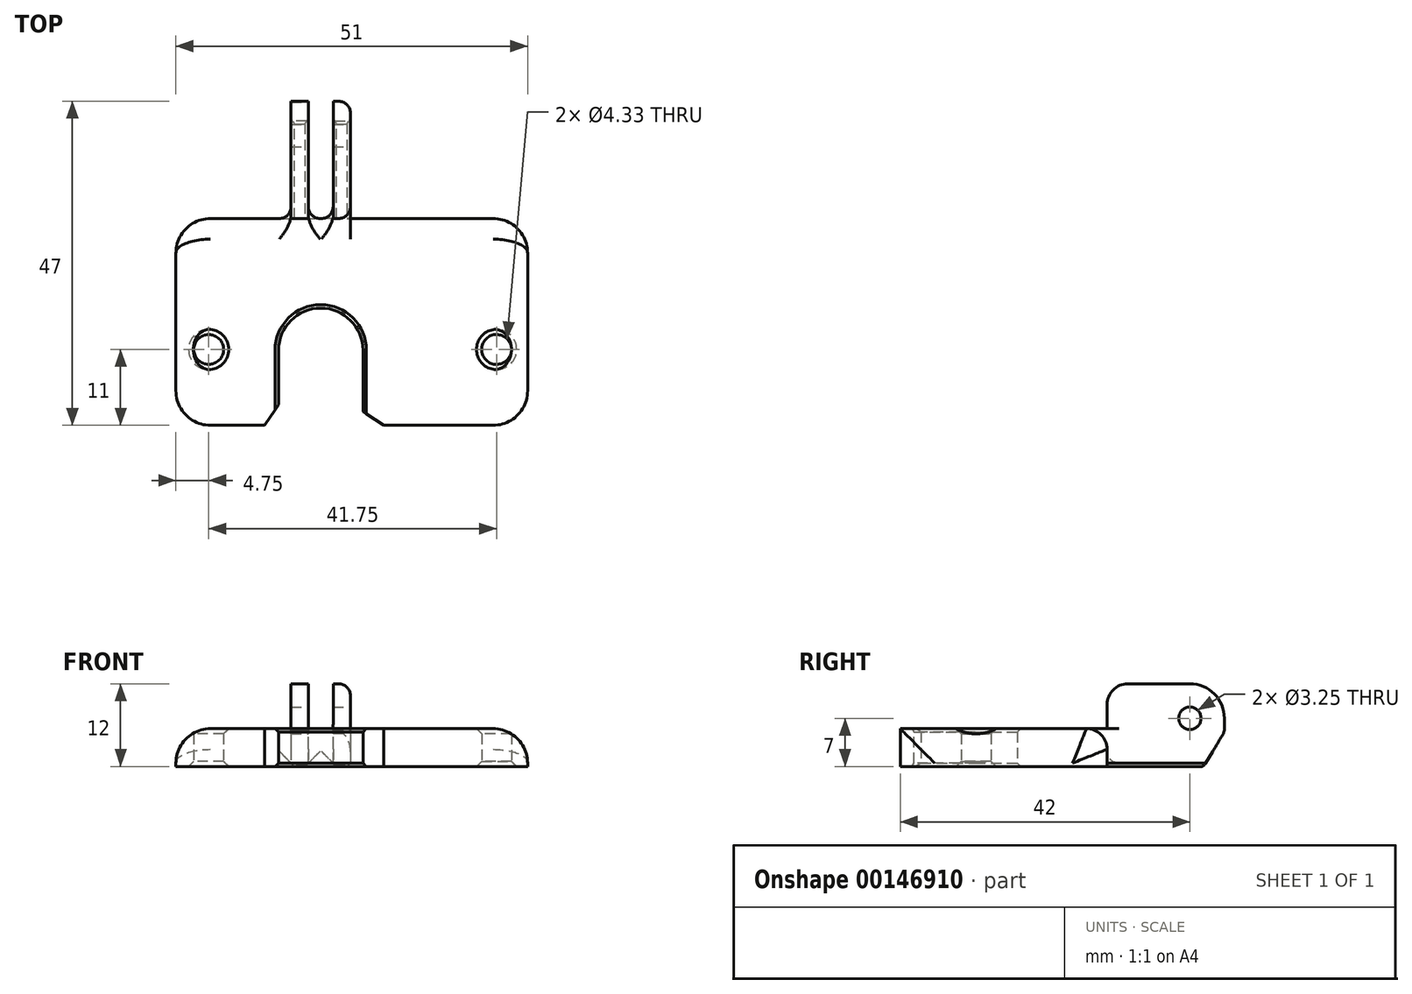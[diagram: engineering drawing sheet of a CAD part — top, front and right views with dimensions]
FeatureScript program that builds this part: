
annotation { "Feature Type Name" : "Feature", "Feature Type Description" : "" }
export const myFeature = defineFeature(function(context is Context, id is Id, definition is map)
    precondition{}
    {
        {
            var Q0;
            Q0=qCreatedBy(makeId("Top.planeOp"),FACE);
            var sketch = newSketch(context, id + "F0", { "sketchPlane" : qUnion([Q0])});
            skLineSegment(sketch, "E0.bottom", {"start": v(-25.5, 11) * mm, "end": v(25.5, 11) * mm});
            skLineSegment(sketch, "E0.top", {"start": v(-25.5, -11) * mm, "end": v(-10.62, -11) * mm});
            skLineSegment(sketch, "E0.left", {"start": v(-25.5, 11) * mm, "end": v(-25.5, -11) * mm});
            skLineSegment(sketch, "E0.right", {"start": v(25.5, 11) * mm, "end": v(25.5, -11) * mm});
            skArc(sketch, "E1", {"start": v(1.63, -0.13) * mm, "mid": v(-4.5, 6) * mm, "end": v(-10.62, -0.13) * mm});
            skLineSegment(sketch, "E2", {"start": v(-10.63, -0.13) * mm, "end": v(-10.62, -11) * mm});
            skLineSegment(sketch, "E3", {"start": v(1.63, -0.13) * mm, "end": v(1.63, -11) * mm});
            skLineSegment(sketch, "E4.trimOffspring", {"start": v(1.63, -11) * mm, "end": v(25.5, -11) * mm});
            skCircle(sketch, "E5", {"center": v(-20.75, 0) * mm, "radius": 2.17 * mm});
            skPoint(sketch, "E6.centerSnap0", {"position": v(-25.5, 0) * mm});
            skCircle(sketch, "E7", {"center": v(21, 0) * mm, "radius": 2.17 * mm});
            skSolve(sketch);
        }
        {
            var Q0;
            Q0 = qSketchRegion(id + "F0", true);
            extrude(context, id + "F1", {"entities" : qUnion([Q0]), "depth" : 5.5 * mm});
        }
        {
            var Q0;
            Q0=makeQuery(id+"F1.opExtrude","CAP_EDGE",EDGE,{"disambiguationData":[OSD([sQuery(id+"F0.wireOp",EDGE,"E5")])],"isStart":true});
            var Q1;
            Q1=makeQuery(id+"F1.opExtrude","CAP_EDGE",EDGE,{"disambiguationData":[OSD([sQuery(id+"F0.wireOp",EDGE,"E7")])],"isStart":true});
            var Q2;
            Q2=makeQuery(id+"F1.opExtrude","CAP_EDGE",EDGE,{"disambiguationData":[OSD([sQuery(id+"F0.wireOp",EDGE,"E7")])],"isStart":false});
            var Q3;
            Q3=makeQuery(id+"F1.opExtrude","CAP_EDGE",EDGE,{"disambiguationData":[OSD([sQuery(id+"F0.wireOp",EDGE,"E5")])],"isStart":false});
            chamfer(context, id + "F2", {"entities" : qUnion([Q0, Q1, Q2, Q3]), "width" : .75 * mm, "tangentPropagation" : true});
        }
        {
            var Q0;
            Q0=qCreatedBy(makeId("Top.planeOp"),FACE);
            var sketch = newSketch(context, id + "F3", { "sketchPlane" : qUnion([Q0])});
            skLineSegment(sketch, "E8.0", {"start": v(-25.5, 11) * mm, "end": v(25.5, 11) * mm});
            skLineSegment(sketch, "E9", {"start": v(-25.5, 11) * mm, "end": v(-25.5, 19) * mm});
            skLineSegment(sketch, "E10", {"start": v(-25.5, 19) * mm, "end": v(25.5, 19) * mm});
            skLineSegment(sketch, "E11", {"start": v(25.5, 19) * mm, "end": v(25.5, 11) * mm});
            skSolve(sketch);
        }
        {
            var Q0;
            Q0 = qSketchRegion(id + "F3", true);
            var Q1;
            Q1=makeQuery(id+"F1.opExtrude","CAP_FACE",FACE,{"disambiguationData":[OSD([sQuery(id+"F0.wireOp",EDGE,"E0.bottom"),sQuery(id+"F0.wireOp",EDGE,"E0.top"),sQuery(id+"F0.wireOp",EDGE,"E0.left"),sQuery(id+"F0.wireOp",EDGE,"E0.right"),sQuery(id+"F0.wireOp",EDGE,"E1"),sQuery(id+"F0.wireOp",EDGE,"E2"),sQuery(id+"F0.wireOp",EDGE,"E3"),sQuery(id+"F0.wireOp",EDGE,"E4.trimOffspring"),sQuery(id+"F0.wireOp",EDGE,"E5"),sQuery(id+"F0.wireOp",EDGE,"E7")])],"isStart":false});
            extrude(context, id + "F4", {"entities" : qUnion([Q0]), "operationType" : NewBodyOperationType.ADD, "endBound" : BoundingType.UP_TO_SURFACE, "endBoundEntityFace" : qUnion([Q1]), "depth" : 6 * mm});
        }
        {
            var Q0;
            Q0=makeQuery(id+"F1.opExtrude","CAP_EDGE",EDGE,{"disambiguationData":[OSD([sQuery(id+"F0.wireOp",EDGE,"E1")])],"isStart":false});
            var Q1;
            Q1=makeQuery(id+"F1.opExtrude","CAP_EDGE",EDGE,{"disambiguationData":[OSD([sQuery(id+"F0.wireOp",EDGE,"E1")])],"isStart":true});
            var Q2;
            Q2=makeQuery(id+"F1.opExtrude","CAP_EDGE",EDGE,{"disambiguationData":[OSD([sQuery(id+"F0.wireOp",EDGE,"E2")])],"isStart":false});
            var Q3;
            {var subQ0=sQuery(id+"F0.wireOp",EDGE,"E7");var subQ1=sQuery(id+"F0.wireOp",EDGE,"E5");var subQ2=sQuery(id+"F0.wireOp",EDGE,"E4.trimOffspring");var subQ3=sQuery(id+"F0.wireOp",EDGE,"E3");var subQ4=sQuery(id+"F0.wireOp",EDGE,"E2");var subQ5=sQuery(id+"F0.wireOp",EDGE,"E1");var subQ6=sQuery(id+"F0.wireOp",EDGE,"E0.right");var subQ7=sQuery(id+"F0.wireOp",EDGE,"E0.left");var subQ8=sQuery(id+"F0.wireOp",EDGE,"E0.top");var subQ9=sQuery(id+"F0.wireOp",EDGE,"E0.bottom");Q3=makeQuery(id+"F15.opChamfer","BLEND_EDGE",EDGE,{"blendedFrom":[makeQuery(id+"F1.opExtrude","SWEPT_EDGE",EDGE,{"disambiguationData":[OSD([subQ8,subQ4])]}),makeQuery(id+"F4.boolean.opBoolean","MERGE",FACE,{"derivedFrom":[makeQuery(id+"F1.opExtrude","CAP_FACE",FACE,{"disambiguationData":[OSD([subQ9,subQ8,subQ7,subQ6,subQ5,subQ4,subQ3,subQ2,subQ1,subQ0])],"isStart":false}),makeQuery(id+"F4.opExtrude","CAP_FACE",FACE,{"disambiguationData":[OSD([subQ9,subQ8,subQ7,subQ6,subQ5,subQ4,subQ3,subQ2,subQ1,subQ0])],"isStart":false})]})],"blendedInto":[makeQuery(id+"F4.boolean.opBoolean","MERGE",FACE,{"derivedFrom":[makeQuery(id+"F1.opExtrude","CAP_FACE",FACE,{"disambiguationData":[OSD([subQ9,subQ8,subQ7,subQ6,subQ5,subQ4,subQ3,subQ2,subQ1,subQ0])],"isStart":false}),makeQuery(id+"F4.opExtrude","CAP_FACE",FACE,{"disambiguationData":[OSD([subQ9,subQ8,subQ7,subQ6,subQ5,subQ4,subQ3,subQ2,subQ1,subQ0])],"isStart":false})]})]});}
            var Q4;
            {var subQ0=sQuery(id+"F0.wireOp",EDGE,"E2");var subQ1=sQuery(id+"F0.wireOp",EDGE,"E0.top");Q4=makeQuery(id+"F15.opChamfer","BLEND_EDGE",EDGE,{"blendedFrom":[makeQuery(id+"F1.opExtrude","SWEPT_EDGE",EDGE,{"disambiguationData":[OSD([subQ1,subQ0])]}),makeQuery(id+"F7.boolean.opBoolean","MERGE",FACE,{"derivedFrom":[makeQuery(id+"F4.boolean.opBoolean","MERGE",FACE,{"derivedFrom":[makeQuery(id+"F1.opExtrude","CAP_FACE",FACE,{"disambiguationData":[OSD([sQuery(id+"F0.wireOp",EDGE,"E0.bottom"),subQ1,sQuery(id+"F0.wireOp",EDGE,"E0.left"),sQuery(id+"F0.wireOp",EDGE,"E0.right"),sQuery(id+"F0.wireOp",EDGE,"E1"),subQ0,sQuery(id+"F0.wireOp",EDGE,"E3"),sQuery(id+"F0.wireOp",EDGE,"E4.trimOffspring"),sQuery(id+"F0.wireOp",EDGE,"E5"),sQuery(id+"F0.wireOp",EDGE,"E7")])],"isStart":true}),makeQuery(id+"F4.opExtrude","CAP_FACE",FACE,{"disambiguationData":[OSD([sQuery(id+"F3.wireOp",EDGE,"E8.0"),sQuery(id+"F3.wireOp",EDGE,"E9"),sQuery(id+"F3.wireOp",EDGE,"E10"),sQuery(id+"F3.wireOp",EDGE,"E11")])],"isStart":true})]}),makeQuery(id+"F7.opExtrude","CAP_FACE",FACE,{"disambiguationData":[OSD([sQuery(id+"F6.wireOp",EDGE,"E15"),sQuery(id+"F6.wireOp",EDGE,"E16"),sQuery(id+"F6.wireOp",EDGE,"E17"),sQuery(id+"F6.wireOp",EDGE,"E18")])],"isStart":true}),makeQuery(id+"F7.opExtrude","CAP_FACE",FACE,{"disambiguationData":[OSD([sQuery(id+"F6.wireOp",EDGE,"E19.MirrorCS"),sQuery(id+"F6.wireOp",EDGE,"E20.MirrorCS"),sQuery(id+"F6.wireOp",EDGE,"E21.MirrorCS"),sQuery(id+"F6.wireOp",EDGE,"E23.MirrorCS")])],"isStart":true})]})],"blendedInto":[makeQuery(id+"F7.boolean.opBoolean","MERGE",FACE,{"derivedFrom":[makeQuery(id+"F4.boolean.opBoolean","MERGE",FACE,{"derivedFrom":[makeQuery(id+"F1.opExtrude","CAP_FACE",FACE,{"disambiguationData":[OSD([sQuery(id+"F0.wireOp",EDGE,"E0.bottom"),subQ1,sQuery(id+"F0.wireOp",EDGE,"E0.left"),sQuery(id+"F0.wireOp",EDGE,"E0.right"),sQuery(id+"F0.wireOp",EDGE,"E1"),subQ0,sQuery(id+"F0.wireOp",EDGE,"E3"),sQuery(id+"F0.wireOp",EDGE,"E4.trimOffspring"),sQuery(id+"F0.wireOp",EDGE,"E5"),sQuery(id+"F0.wireOp",EDGE,"E7")])],"isStart":true}),makeQuery(id+"F4.opExtrude","CAP_FACE",FACE,{"disambiguationData":[OSD([sQuery(id+"F3.wireOp",EDGE,"E8.0"),sQuery(id+"F3.wireOp",EDGE,"E9"),sQuery(id+"F3.wireOp",EDGE,"E10"),sQuery(id+"F3.wireOp",EDGE,"E11")])],"isStart":true})]}),makeQuery(id+"F7.opExtrude","CAP_FACE",FACE,{"disambiguationData":[OSD([sQuery(id+"F6.wireOp",EDGE,"E15"),sQuery(id+"F6.wireOp",EDGE,"E16"),sQuery(id+"F6.wireOp",EDGE,"E17"),sQuery(id+"F6.wireOp",EDGE,"E18")])],"isStart":true}),makeQuery(id+"F7.opExtrude","CAP_FACE",FACE,{"disambiguationData":[OSD([sQuery(id+"F6.wireOp",EDGE,"E19.MirrorCS"),sQuery(id+"F6.wireOp",EDGE,"E20.MirrorCS"),sQuery(id+"F6.wireOp",EDGE,"E21.MirrorCS"),sQuery(id+"F6.wireOp",EDGE,"E23.MirrorCS")])],"isStart":true})]})]});}
            var Q5;
            Q5=makeQuery(id+"F1.opExtrude","CAP_EDGE",EDGE,{"disambiguationData":[OSD([sQuery(id+"F0.wireOp",EDGE,"E2")])],"isStart":true});
            var Q6;
            Q6=makeQuery(id+"F1.opExtrude","CAP_EDGE",EDGE,{"disambiguationData":[OSD([sQuery(id+"F0.wireOp",EDGE,"E3")])],"isStart":true});
            var Q7;
            {var subQ0=sQuery(id+"F0.wireOp",EDGE,"E4.trimOffspring");var subQ1=sQuery(id+"F0.wireOp",EDGE,"E3");Q7=makeQuery(id+"F15.opChamfer","BLEND_EDGE",EDGE,{"blendedFrom":[makeQuery(id+"F1.opExtrude","SWEPT_EDGE",EDGE,{"disambiguationData":[OSD([subQ1,subQ0])]}),makeQuery(id+"F7.boolean.opBoolean","MERGE",FACE,{"derivedFrom":[makeQuery(id+"F4.boolean.opBoolean","MERGE",FACE,{"derivedFrom":[makeQuery(id+"F1.opExtrude","CAP_FACE",FACE,{"disambiguationData":[OSD([sQuery(id+"F0.wireOp",EDGE,"E0.bottom"),sQuery(id+"F0.wireOp",EDGE,"E0.top"),sQuery(id+"F0.wireOp",EDGE,"E0.left"),sQuery(id+"F0.wireOp",EDGE,"E0.right"),sQuery(id+"F0.wireOp",EDGE,"E1"),sQuery(id+"F0.wireOp",EDGE,"E2"),subQ1,subQ0,sQuery(id+"F0.wireOp",EDGE,"E5"),sQuery(id+"F0.wireOp",EDGE,"E7")])],"isStart":true}),makeQuery(id+"F4.opExtrude","CAP_FACE",FACE,{"disambiguationData":[OSD([sQuery(id+"F3.wireOp",EDGE,"E8.0"),sQuery(id+"F3.wireOp",EDGE,"E9"),sQuery(id+"F3.wireOp",EDGE,"E10"),sQuery(id+"F3.wireOp",EDGE,"E11")])],"isStart":true})]}),makeQuery(id+"F7.opExtrude","CAP_FACE",FACE,{"disambiguationData":[OSD([sQuery(id+"F6.wireOp",EDGE,"E15"),sQuery(id+"F6.wireOp",EDGE,"E16"),sQuery(id+"F6.wireOp",EDGE,"E17"),sQuery(id+"F6.wireOp",EDGE,"E18")])],"isStart":true}),makeQuery(id+"F7.opExtrude","CAP_FACE",FACE,{"disambiguationData":[OSD([sQuery(id+"F6.wireOp",EDGE,"E19.MirrorCS"),sQuery(id+"F6.wireOp",EDGE,"E20.MirrorCS"),sQuery(id+"F6.wireOp",EDGE,"E21.MirrorCS"),sQuery(id+"F6.wireOp",EDGE,"E23.MirrorCS")])],"isStart":true})]})],"blendedInto":[makeQuery(id+"F7.boolean.opBoolean","MERGE",FACE,{"derivedFrom":[makeQuery(id+"F4.boolean.opBoolean","MERGE",FACE,{"derivedFrom":[makeQuery(id+"F1.opExtrude","CAP_FACE",FACE,{"disambiguationData":[OSD([sQuery(id+"F0.wireOp",EDGE,"E0.bottom"),sQuery(id+"F0.wireOp",EDGE,"E0.top"),sQuery(id+"F0.wireOp",EDGE,"E0.left"),sQuery(id+"F0.wireOp",EDGE,"E0.right"),sQuery(id+"F0.wireOp",EDGE,"E1"),sQuery(id+"F0.wireOp",EDGE,"E2"),subQ1,subQ0,sQuery(id+"F0.wireOp",EDGE,"E5"),sQuery(id+"F0.wireOp",EDGE,"E7")])],"isStart":true}),makeQuery(id+"F4.opExtrude","CAP_FACE",FACE,{"disambiguationData":[OSD([sQuery(id+"F3.wireOp",EDGE,"E8.0"),sQuery(id+"F3.wireOp",EDGE,"E9"),sQuery(id+"F3.wireOp",EDGE,"E10"),sQuery(id+"F3.wireOp",EDGE,"E11")])],"isStart":true})]}),makeQuery(id+"F7.opExtrude","CAP_FACE",FACE,{"disambiguationData":[OSD([sQuery(id+"F6.wireOp",EDGE,"E15"),sQuery(id+"F6.wireOp",EDGE,"E16"),sQuery(id+"F6.wireOp",EDGE,"E17"),sQuery(id+"F6.wireOp",EDGE,"E18")])],"isStart":true}),makeQuery(id+"F7.opExtrude","CAP_FACE",FACE,{"disambiguationData":[OSD([sQuery(id+"F6.wireOp",EDGE,"E19.MirrorCS"),sQuery(id+"F6.wireOp",EDGE,"E20.MirrorCS"),sQuery(id+"F6.wireOp",EDGE,"E21.MirrorCS"),sQuery(id+"F6.wireOp",EDGE,"E23.MirrorCS")])],"isStart":true})]})]});}
            var Q8;
            Q8=makeQuery(id+"F1.opExtrude","CAP_EDGE",EDGE,{"disambiguationData":[OSD([sQuery(id+"F0.wireOp",EDGE,"E3")])],"isStart":false});
            var Q9;
            {var subQ0=sQuery(id+"F0.wireOp",EDGE,"E7");var subQ1=sQuery(id+"F0.wireOp",EDGE,"E5");var subQ2=sQuery(id+"F0.wireOp",EDGE,"E4.trimOffspring");var subQ3=sQuery(id+"F0.wireOp",EDGE,"E3");var subQ4=sQuery(id+"F0.wireOp",EDGE,"E2");var subQ5=sQuery(id+"F0.wireOp",EDGE,"E1");var subQ6=sQuery(id+"F0.wireOp",EDGE,"E0.right");var subQ7=sQuery(id+"F0.wireOp",EDGE,"E0.left");var subQ8=sQuery(id+"F0.wireOp",EDGE,"E0.top");var subQ9=sQuery(id+"F0.wireOp",EDGE,"E0.bottom");Q9=makeQuery(id+"F15.opChamfer","BLEND_EDGE",EDGE,{"blendedFrom":[makeQuery(id+"F1.opExtrude","SWEPT_EDGE",EDGE,{"disambiguationData":[OSD([subQ3,subQ2])]}),makeQuery(id+"F4.boolean.opBoolean","MERGE",FACE,{"derivedFrom":[makeQuery(id+"F1.opExtrude","CAP_FACE",FACE,{"disambiguationData":[OSD([subQ9,subQ8,subQ7,subQ6,subQ5,subQ4,subQ3,subQ2,subQ1,subQ0])],"isStart":false}),makeQuery(id+"F4.opExtrude","CAP_FACE",FACE,{"disambiguationData":[OSD([subQ9,subQ8,subQ7,subQ6,subQ5,subQ4,subQ3,subQ2,subQ1,subQ0])],"isStart":false})]})],"blendedInto":[makeQuery(id+"F4.boolean.opBoolean","MERGE",FACE,{"derivedFrom":[makeQuery(id+"F1.opExtrude","CAP_FACE",FACE,{"disambiguationData":[OSD([subQ9,subQ8,subQ7,subQ6,subQ5,subQ4,subQ3,subQ2,subQ1,subQ0])],"isStart":false}),makeQuery(id+"F4.opExtrude","CAP_FACE",FACE,{"disambiguationData":[OSD([subQ9,subQ8,subQ7,subQ6,subQ5,subQ4,subQ3,subQ2,subQ1,subQ0])],"isStart":false})]})]});}
            chamfer(context, id + "F5", {"entities" : qUnion([Q0, Q1, Q2, Q3, Q4, Q5, Q6, Q7, Q8, Q9]), "width" : .5 * mm, "tangentPropagation" : true});
        }
        {
            var Q0;
            Q0=qCreatedBy(makeId("Top.planeOp"),FACE);
            var sketch = newSketch(context, id + "F6", { "sketchPlane" : qUnion([Q0])});
            skArc(sketch, "E12.0", {"start": v(1.63, -0.13) * mm, "mid": v(-4.5, 6) * mm, "end": v(-10.62, -0.13) * mm, "construction": true});
            skLineSegment(sketch, "E13.0", {"start": v(-25.5, 19) * mm, "end": v(25.5, 19) * mm, "construction": true});
            skLineSegment(sketch, "E14", {"start": v(-4.5, 32.8) * mm, "end": v(-4.5, -0.13) * mm, "construction": true});
            skLineSegment(sketch, "E15", {"start": v(-8.8, 36) * mm, "end": v(-6.3, 36) * mm});
            skLineSegment(sketch, "E16", {"start": v(-6.3, 36) * mm, "end": v(-6.3, 19) * mm});
            skLineSegment(sketch, "E17", {"start": v(-6.3, 19) * mm, "end": v(-8.8, 19) * mm});
            skLineSegment(sketch, "E18", {"start": v(-8.8, 19) * mm, "end": v(-8.8, 36) * mm});
            skLineSegment(sketch, "E19.MirrorCS", {"start": v(-2.7, 36) * mm, "end": v(-2.7, 19) * mm});
            skLineSegment(sketch, "E20.MirrorCS", {"start": v(-0.2, 19) * mm, "end": v(-0.2, 36) * mm});
            skLineSegment(sketch, "E21.MirrorCS", {"start": v(-0.2, 36) * mm, "end": v(-2.7, 36) * mm});
            skLineSegment(sketch, "E22.MirrorCS", {"start": v(-4.5, 5.2) * mm, "end": v(-4.5, 38.13) * mm, "construction": true});
            skLineSegment(sketch, "E23.MirrorCS", {"start": v(-2.7, 19) * mm, "end": v(-0.2, 19) * mm});
            skSolve(sketch);
        }
        {
            var Q0;
            Q0 = qSketchRegion(id + "F6", true);
            extrude(context, id + "F7", {"entities" : qUnion([Q0]), "operationType" : NewBodyOperationType.ADD, "depth" : 12 * mm});
        }
        {
            var Q0;
            Q0=makeQuery(id+"F7.opExtrude","SWEPT_FACE",FACE,{"disambiguationData":[OSD([sQuery(id+"F6.wireOp",EDGE,"E20.MirrorCS")])]});
            var sketch = newSketch(context, id + "F8", { "sketchPlane" : qUnion([Q0])});
            skCircle(sketch, "E24", {"center": v(31, 7) * mm, "radius": 1.63 * mm});
            skLineSegment(sketch, "E25.0", {"start": v(36, 12) * mm, "end": v(36, 0) * mm, "construction": true});
            skLineSegment(sketch, "E26.0", {"start": v(19, 0) * mm, "end": v(36, 0) * mm, "construction": true});
            skSolve(sketch);
        }
        {
            var Q0;
            Q0 = qSketchRegion(id + "F8", true);
            extrude(context, id + "F9", {"entities" : qUnion([Q0]), "operationType" : NewBodyOperationType.REMOVE, "endBound" : BoundingType.THROUGH_ALL, "oppositeDirection" : true, "depth" : 25 * mm});
        }
        {
            var Q0;
            Q0=makeQuery(id+"F7.opExtrude","CAP_EDGE",EDGE,{"disambiguationData":[OSD([sQuery(id+"F6.wireOp",EDGE,"E23.MirrorCS")])],"isStart":false});
            var Q1;
            Q1=makeQuery(id+"F7.opExtrude","CAP_EDGE",EDGE,{"disambiguationData":[OSD([sQuery(id+"F6.wireOp",EDGE,"E17")])],"isStart":false});
            var Q2;
            {var subQ0=sQuery(id+"F3.wireOp",EDGE,"E10");Q2=makeQuery(id+"F7.boolean.opBoolean","SPLIT",EDGE,{"disambiguationData":[topologyDisambiguationEdgeConnected([makeQuery(id+"F1.opExtrude","CAP_FACE",FACE,{"disambiguationData":[OSD([sQuery(id+"F0.wireOp",EDGE,"E0.bottom"),sQuery(id+"F0.wireOp",EDGE,"E0.top"),sQuery(id+"F0.wireOp",EDGE,"E0.left"),sQuery(id+"F0.wireOp",EDGE,"E0.right"),sQuery(id+"F0.wireOp",EDGE,"E1"),sQuery(id+"F0.wireOp",EDGE,"E2"),sQuery(id+"F0.wireOp",EDGE,"E3"),sQuery(id+"F0.wireOp",EDGE,"E4.trimOffspring"),sQuery(id+"F0.wireOp",EDGE,"E5"),sQuery(id+"F0.wireOp",EDGE,"E7")])],"isStart":false}),makeQuery(id+"F4.opExtrude","CAP_FACE",FACE,{"disambiguationData":[OSD([sQuery(id+"F3.wireOp",EDGE,"E8.0"),sQuery(id+"F3.wireOp",EDGE,"E9"),subQ0,sQuery(id+"F3.wireOp",EDGE,"E11")])],"isStart":false}),makeQuery(id+"F7.opExtrude","SWEPT_FACE",FACE,{"disambiguationData":[OSD([sQuery(id+"F6.wireOp",EDGE,"E23.MirrorCS")])]})])],"derivedFrom":makeQuery(id+"F4.opExtrude","CAP_EDGE",EDGE,{"disambiguationData":[OSD([subQ0])],"isStart":false})});}
            var Q3;
            {var subQ0=sQuery(id+"F3.wireOp",EDGE,"E10");Q3=makeQuery(id+"F7.boolean.opBoolean","SPLIT",EDGE,{"disambiguationData":[topologyDisambiguationEdgeConnected([makeQuery(id+"F1.opExtrude","CAP_FACE",FACE,{"disambiguationData":[OSD([sQuery(id+"F0.wireOp",EDGE,"E0.bottom"),sQuery(id+"F0.wireOp",EDGE,"E0.top"),sQuery(id+"F0.wireOp",EDGE,"E0.left"),sQuery(id+"F0.wireOp",EDGE,"E0.right"),sQuery(id+"F0.wireOp",EDGE,"E1"),sQuery(id+"F0.wireOp",EDGE,"E2"),sQuery(id+"F0.wireOp",EDGE,"E3"),sQuery(id+"F0.wireOp",EDGE,"E4.trimOffspring"),sQuery(id+"F0.wireOp",EDGE,"E5"),sQuery(id+"F0.wireOp",EDGE,"E7")])],"isStart":false}),makeQuery(id+"F4.opExtrude","CAP_FACE",FACE,{"disambiguationData":[OSD([sQuery(id+"F3.wireOp",EDGE,"E8.0"),sQuery(id+"F3.wireOp",EDGE,"E9"),subQ0,sQuery(id+"F3.wireOp",EDGE,"E11")])],"isStart":false}),makeQuery(id+"F7.opExtrude","SWEPT_FACE",FACE,{"disambiguationData":[OSD([sQuery(id+"F6.wireOp",EDGE,"E17")])]})])],"derivedFrom":makeQuery(id+"F4.opExtrude","CAP_EDGE",EDGE,{"disambiguationData":[OSD([subQ0])],"isStart":false})});}
            fillet(context, id + "F10", {"entities" : qUnion([Q0, Q1, Q2, Q3]), "radius" : 3 * mm, "tangentPropagation" : true, "allowEdgeOverflow" : false});
        }
        {
            var Q0;
            Q0=makeQuery(id+"F7.opExtrude","CAP_EDGE",EDGE,{"disambiguationData":[OSD([sQuery(id+"F6.wireOp",EDGE,"E21.MirrorCS")])],"isStart":false});
            var Q1;
            Q1=makeQuery(id+"F7.opExtrude","CAP_EDGE",EDGE,{"disambiguationData":[OSD([sQuery(id+"F6.wireOp",EDGE,"E15")])],"isStart":false});
            fillet(context, id + "F11", {"entities" : qUnion([Q0, Q1]), "radius" : 5 * mm, "tangentPropagation" : true, "allowEdgeOverflow" : false});
        }
        {
            var Q0;
            Q0=makeQuery(id+"F7.opExtrude","CAP_EDGE",EDGE,{"disambiguationData":[OSD([sQuery(id+"F6.wireOp",EDGE,"E21.MirrorCS")])],"isStart":true});
            var Q1;
            Q1=makeQuery(id+"F7.opExtrude","CAP_EDGE",EDGE,{"disambiguationData":[OSD([sQuery(id+"F6.wireOp",EDGE,"E15")])],"isStart":true});
            chamfer(context, id + "F12", {"entities" : qUnion([Q0, Q1]), "chamferType" : ChamferType.TWO_OFFSETS, "width1" : 5 * mm, "oppositeDirection" : false, "width2" : 3 * mm, "tangentPropagation" : true});
        }
        {
            var Q0;
            {var subQ0=sQuery(id+"F6.wireOp",EDGE,"E21.MirrorCS");Q0=makeQuery(id+"F12.opChamfer","BLEND_EDGE",EDGE,{"blendedFrom":[makeQuery(id+"F7.opExtrude","CAP_EDGE",EDGE,{"disambiguationData":[OSD([subQ0])],"isStart":true}),makeQuery(id+"F7.opExtrude","SWEPT_FACE",FACE,{"disambiguationData":[OSD([subQ0])]})],"blendedInto":[makeQuery(id+"F7.opExtrude","SWEPT_FACE",FACE,{"disambiguationData":[OSD([subQ0])]})]});}
            var Q1;
            {var subQ0=sQuery(id+"F6.wireOp",EDGE,"E15");Q1=makeQuery(id+"F12.opChamfer","BLEND_EDGE",EDGE,{"blendedFrom":[makeQuery(id+"F7.opExtrude","CAP_EDGE",EDGE,{"disambiguationData":[OSD([subQ0])],"isStart":true}),makeQuery(id+"F7.opExtrude","SWEPT_FACE",FACE,{"disambiguationData":[OSD([subQ0])]})],"blendedInto":[makeQuery(id+"F7.opExtrude","SWEPT_FACE",FACE,{"disambiguationData":[OSD([subQ0])]})]});}
            chamfer(context, id + "F13", {"entities" : qUnion([Q0, Q1]), "width" : 1 * mm, "tangentPropagation" : true});
        }
        {
            var Q0;
            Q0=makeQuery(id+"F1.opExtrude","SWEPT_EDGE",EDGE,{"disambiguationData":[OSD([sQuery(id+"F0.wireOp",EDGE,"E0.right"),sQuery(id+"F0.wireOp",EDGE,"E4.trimOffspring")])]});
            var Q1;
            Q1=makeQuery(id+"F1.opExtrude","SWEPT_EDGE",EDGE,{"disambiguationData":[OSD([sQuery(id+"F0.wireOp",EDGE,"E0.top"),sQuery(id+"F0.wireOp",EDGE,"E0.left")])]});
            var Q2;
            Q2=makeQuery(id+"F4.opExtrude","SWEPT_EDGE",EDGE,{"disambiguationData":[OSD([sQuery(id+"F3.wireOp",EDGE,"E10"),sQuery(id+"F3.wireOp",EDGE,"E11")])]});
            var Q3;
            Q3=makeQuery(id+"F4.opExtrude","SWEPT_EDGE",EDGE,{"disambiguationData":[OSD([sQuery(id+"F3.wireOp",EDGE,"E9"),sQuery(id+"F3.wireOp",EDGE,"E10")])]});
            fillet(context, id + "F14", {"entities" : qUnion([Q0, Q1, Q2, Q3]), "radius" : 5 * mm, "tangentPropagation" : true, "allowEdgeOverflow" : false});
        }
        {
            var Q0;
            Q0=makeQuery(id+"F1.opExtrude","SWEPT_EDGE",EDGE,{"disambiguationData":[OSD([sQuery(id+"F0.wireOp",EDGE,"E0.top"),sQuery(id+"F0.wireOp",EDGE,"E2")])]});
            var Q1;
            Q1=makeQuery(id+"F1.opExtrude","SWEPT_EDGE",EDGE,{"disambiguationData":[OSD([sQuery(id+"F0.wireOp",EDGE,"E3"),sQuery(id+"F0.wireOp",EDGE,"E4.trimOffspring")])]});
            chamfer(context, id + "F15", {"entities" : qUnion([Q0, Q1]), "chamferType" : ChamferType.TWO_OFFSETS, "width1" : 3 * mm, "oppositeDirection" : false, "width2" : 2 * mm, "tangentPropagation" : true});
        }
        {
            var Q0;
            Q0=makeQuery(id+"F7.opExtrude","CAP_EDGE",EDGE,{"disambiguationData":[OSD([sQuery(id+"F6.wireOp",EDGE,"E20.MirrorCS")])],"isStart":true});
            var Q1;
            {var subQ0=sQuery(id+"F6.wireOp",EDGE,"E21.MirrorCS");Q1=makeQuery(id+"F12.opChamfer","BLEND_EDGE",EDGE,{"blendedFrom":[makeQuery(id+"F7.opExtrude","CAP_EDGE",EDGE,{"disambiguationData":[OSD([subQ0])],"isStart":true}),makeQuery(id+"F7.boolean.opBoolean","MERGE",FACE,{"derivedFrom":[makeQuery(id+"F4.boolean.opBoolean","MERGE",FACE,{"derivedFrom":[makeQuery(id+"F1.opExtrude","CAP_FACE",FACE,{"disambiguationData":[OSD([sQuery(id+"F0.wireOp",EDGE,"E0.bottom"),sQuery(id+"F0.wireOp",EDGE,"E0.top"),sQuery(id+"F0.wireOp",EDGE,"E0.left"),sQuery(id+"F0.wireOp",EDGE,"E0.right"),sQuery(id+"F0.wireOp",EDGE,"E1"),sQuery(id+"F0.wireOp",EDGE,"E2"),sQuery(id+"F0.wireOp",EDGE,"E3"),sQuery(id+"F0.wireOp",EDGE,"E4.trimOffspring"),sQuery(id+"F0.wireOp",EDGE,"E5"),sQuery(id+"F0.wireOp",EDGE,"E7")])],"isStart":true}),makeQuery(id+"F4.opExtrude","CAP_FACE",FACE,{"disambiguationData":[OSD([sQuery(id+"F3.wireOp",EDGE,"E8.0"),sQuery(id+"F3.wireOp",EDGE,"E9"),sQuery(id+"F3.wireOp",EDGE,"E10"),sQuery(id+"F3.wireOp",EDGE,"E11")])],"isStart":true})]}),makeQuery(id+"F7.opExtrude","CAP_FACE",FACE,{"disambiguationData":[OSD([sQuery(id+"F6.wireOp",EDGE,"E15"),sQuery(id+"F6.wireOp",EDGE,"E16"),sQuery(id+"F6.wireOp",EDGE,"E17"),sQuery(id+"F6.wireOp",EDGE,"E18")])],"isStart":true}),makeQuery(id+"F7.opExtrude","CAP_FACE",FACE,{"disambiguationData":[OSD([sQuery(id+"F6.wireOp",EDGE,"E19.MirrorCS"),sQuery(id+"F6.wireOp",EDGE,"E20.MirrorCS"),subQ0,sQuery(id+"F6.wireOp",EDGE,"E23.MirrorCS")])],"isStart":true})]})],"blendedInto":[makeQuery(id+"F7.boolean.opBoolean","MERGE",FACE,{"derivedFrom":[makeQuery(id+"F4.boolean.opBoolean","MERGE",FACE,{"derivedFrom":[makeQuery(id+"F1.opExtrude","CAP_FACE",FACE,{"disambiguationData":[OSD([sQuery(id+"F0.wireOp",EDGE,"E0.bottom"),sQuery(id+"F0.wireOp",EDGE,"E0.top"),sQuery(id+"F0.wireOp",EDGE,"E0.left"),sQuery(id+"F0.wireOp",EDGE,"E0.right"),sQuery(id+"F0.wireOp",EDGE,"E1"),sQuery(id+"F0.wireOp",EDGE,"E2"),sQuery(id+"F0.wireOp",EDGE,"E3"),sQuery(id+"F0.wireOp",EDGE,"E4.trimOffspring"),sQuery(id+"F0.wireOp",EDGE,"E5"),sQuery(id+"F0.wireOp",EDGE,"E7")])],"isStart":true}),makeQuery(id+"F4.opExtrude","CAP_FACE",FACE,{"disambiguationData":[OSD([sQuery(id+"F3.wireOp",EDGE,"E8.0"),sQuery(id+"F3.wireOp",EDGE,"E9"),sQuery(id+"F3.wireOp",EDGE,"E10"),sQuery(id+"F3.wireOp",EDGE,"E11")])],"isStart":true})]}),makeQuery(id+"F7.opExtrude","CAP_FACE",FACE,{"disambiguationData":[OSD([sQuery(id+"F6.wireOp",EDGE,"E15"),sQuery(id+"F6.wireOp",EDGE,"E16"),sQuery(id+"F6.wireOp",EDGE,"E17"),sQuery(id+"F6.wireOp",EDGE,"E18")])],"isStart":true}),makeQuery(id+"F7.opExtrude","CAP_FACE",FACE,{"disambiguationData":[OSD([sQuery(id+"F6.wireOp",EDGE,"E19.MirrorCS"),sQuery(id+"F6.wireOp",EDGE,"E20.MirrorCS"),subQ0,sQuery(id+"F6.wireOp",EDGE,"E23.MirrorCS")])],"isStart":true})]})]});}
            var Q2;
            Q2=makeQuery(id+"F7.opExtrude","CAP_EDGE",EDGE,{"disambiguationData":[OSD([sQuery(id+"F6.wireOp",EDGE,"E19.MirrorCS")])],"isStart":true});
            var Q3;
            Q3=makeQuery(id+"F7.opExtrude","CAP_EDGE",EDGE,{"disambiguationData":[OSD([sQuery(id+"F6.wireOp",EDGE,"E16")])],"isStart":true});
            var Q4;
            Q4=makeQuery(id+"F7.opExtrude","CAP_EDGE",EDGE,{"disambiguationData":[OSD([sQuery(id+"F6.wireOp",EDGE,"E18")])],"isStart":true});
            var Q5;
            {var subQ0=sQuery(id+"F6.wireOp",EDGE,"E15");Q5=makeQuery(id+"F12.opChamfer","BLEND_EDGE",EDGE,{"blendedFrom":[makeQuery(id+"F7.opExtrude","CAP_EDGE",EDGE,{"disambiguationData":[OSD([subQ0])],"isStart":true}),makeQuery(id+"F7.boolean.opBoolean","MERGE",FACE,{"derivedFrom":[makeQuery(id+"F4.boolean.opBoolean","MERGE",FACE,{"derivedFrom":[makeQuery(id+"F1.opExtrude","CAP_FACE",FACE,{"disambiguationData":[OSD([sQuery(id+"F0.wireOp",EDGE,"E0.bottom"),sQuery(id+"F0.wireOp",EDGE,"E0.top"),sQuery(id+"F0.wireOp",EDGE,"E0.left"),sQuery(id+"F0.wireOp",EDGE,"E0.right"),sQuery(id+"F0.wireOp",EDGE,"E1"),sQuery(id+"F0.wireOp",EDGE,"E2"),sQuery(id+"F0.wireOp",EDGE,"E3"),sQuery(id+"F0.wireOp",EDGE,"E4.trimOffspring"),sQuery(id+"F0.wireOp",EDGE,"E5"),sQuery(id+"F0.wireOp",EDGE,"E7")])],"isStart":true}),makeQuery(id+"F4.opExtrude","CAP_FACE",FACE,{"disambiguationData":[OSD([sQuery(id+"F3.wireOp",EDGE,"E8.0"),sQuery(id+"F3.wireOp",EDGE,"E9"),sQuery(id+"F3.wireOp",EDGE,"E10"),sQuery(id+"F3.wireOp",EDGE,"E11")])],"isStart":true})]}),makeQuery(id+"F7.opExtrude","CAP_FACE",FACE,{"disambiguationData":[OSD([subQ0,sQuery(id+"F6.wireOp",EDGE,"E16"),sQuery(id+"F6.wireOp",EDGE,"E17"),sQuery(id+"F6.wireOp",EDGE,"E18")])],"isStart":true}),makeQuery(id+"F7.opExtrude","CAP_FACE",FACE,{"disambiguationData":[OSD([sQuery(id+"F6.wireOp",EDGE,"E19.MirrorCS"),sQuery(id+"F6.wireOp",EDGE,"E20.MirrorCS"),sQuery(id+"F6.wireOp",EDGE,"E21.MirrorCS"),sQuery(id+"F6.wireOp",EDGE,"E23.MirrorCS")])],"isStart":true})]})],"blendedInto":[makeQuery(id+"F7.boolean.opBoolean","MERGE",FACE,{"derivedFrom":[makeQuery(id+"F4.boolean.opBoolean","MERGE",FACE,{"derivedFrom":[makeQuery(id+"F1.opExtrude","CAP_FACE",FACE,{"disambiguationData":[OSD([sQuery(id+"F0.wireOp",EDGE,"E0.bottom"),sQuery(id+"F0.wireOp",EDGE,"E0.top"),sQuery(id+"F0.wireOp",EDGE,"E0.left"),sQuery(id+"F0.wireOp",EDGE,"E0.right"),sQuery(id+"F0.wireOp",EDGE,"E1"),sQuery(id+"F0.wireOp",EDGE,"E2"),sQuery(id+"F0.wireOp",EDGE,"E3"),sQuery(id+"F0.wireOp",EDGE,"E4.trimOffspring"),sQuery(id+"F0.wireOp",EDGE,"E5"),sQuery(id+"F0.wireOp",EDGE,"E7")])],"isStart":true}),makeQuery(id+"F4.opExtrude","CAP_FACE",FACE,{"disambiguationData":[OSD([sQuery(id+"F3.wireOp",EDGE,"E8.0"),sQuery(id+"F3.wireOp",EDGE,"E9"),sQuery(id+"F3.wireOp",EDGE,"E10"),sQuery(id+"F3.wireOp",EDGE,"E11")])],"isStart":true})]}),makeQuery(id+"F7.opExtrude","CAP_FACE",FACE,{"disambiguationData":[OSD([subQ0,sQuery(id+"F6.wireOp",EDGE,"E16"),sQuery(id+"F6.wireOp",EDGE,"E17"),sQuery(id+"F6.wireOp",EDGE,"E18")])],"isStart":true}),makeQuery(id+"F7.opExtrude","CAP_FACE",FACE,{"disambiguationData":[OSD([sQuery(id+"F6.wireOp",EDGE,"E19.MirrorCS"),sQuery(id+"F6.wireOp",EDGE,"E20.MirrorCS"),sQuery(id+"F6.wireOp",EDGE,"E21.MirrorCS"),sQuery(id+"F6.wireOp",EDGE,"E23.MirrorCS")])],"isStart":true})]})]});}
            chamfer(context, id + "F16", {"entities" : qUnion([Q0, Q1, Q2, Q3, Q4, Q5]), "width" : .5 * mm, "tangentPropagation" : true});
        }
        {
            var Q0;
            {var subQ0=sQuery(id+"F6.wireOp",EDGE,"E18");Q0=makeQuery(id+"F7.boolean.opBoolean","SPLIT",EDGE,{"disambiguationData":[topologyDisambiguationEdgeConnected([makeQuery(id+"F4.opExtrude","SWEPT_FACE",FACE,{"disambiguationData":[OSD([sQuery(id+"F3.wireOp",EDGE,"E10")])]})])],"derivedFrom":makeQuery(id+"F7.opExtrude","SWEPT_EDGE",EDGE,{"disambiguationData":[OSD([sQuery(id+"F6.wireOp",EDGE,"E17"),subQ0])]})});}
            var Q1;
            {var subQ0=sQuery(id+"F6.wireOp",EDGE,"E16");Q1=makeQuery(id+"F7.boolean.opBoolean","SPLIT",EDGE,{"disambiguationData":[topologyDisambiguationEdgeConnected([makeQuery(id+"F4.opExtrude","SWEPT_FACE",FACE,{"disambiguationData":[OSD([sQuery(id+"F3.wireOp",EDGE,"E10")])]})])],"derivedFrom":makeQuery(id+"F7.opExtrude","SWEPT_EDGE",EDGE,{"disambiguationData":[OSD([subQ0,sQuery(id+"F6.wireOp",EDGE,"E17")])]})});}
            var Q2;
            {var subQ0=sQuery(id+"F6.wireOp",EDGE,"E19.MirrorCS");Q2=makeQuery(id+"F7.boolean.opBoolean","SPLIT",EDGE,{"disambiguationData":[topologyDisambiguationEdgeConnected([makeQuery(id+"F4.opExtrude","SWEPT_FACE",FACE,{"disambiguationData":[OSD([sQuery(id+"F3.wireOp",EDGE,"E10")])]})])],"derivedFrom":makeQuery(id+"F7.opExtrude","SWEPT_EDGE",EDGE,{"disambiguationData":[OSD([subQ0,sQuery(id+"F6.wireOp",EDGE,"E23.MirrorCS")])]})});}
            var Q3;
            {var subQ0=sQuery(id+"F6.wireOp",EDGE,"E20.MirrorCS");Q3=makeQuery(id+"F7.boolean.opBoolean","SPLIT",EDGE,{"disambiguationData":[topologyDisambiguationEdgeConnected([makeQuery(id+"F4.opExtrude","SWEPT_FACE",FACE,{"disambiguationData":[OSD([sQuery(id+"F3.wireOp",EDGE,"E10")])]})])],"derivedFrom":makeQuery(id+"F7.opExtrude","SWEPT_EDGE",EDGE,{"disambiguationData":[OSD([subQ0,sQuery(id+"F6.wireOp",EDGE,"E23.MirrorCS")])]})});}
            fillet(context, id + "F17", {"entities" : qUnion([Q0, Q1, Q2, Q3]), "radius" : 1.7 * mm, "tangentPropagation" : true, "allowEdgeOverflow" : false});
        }
    });
